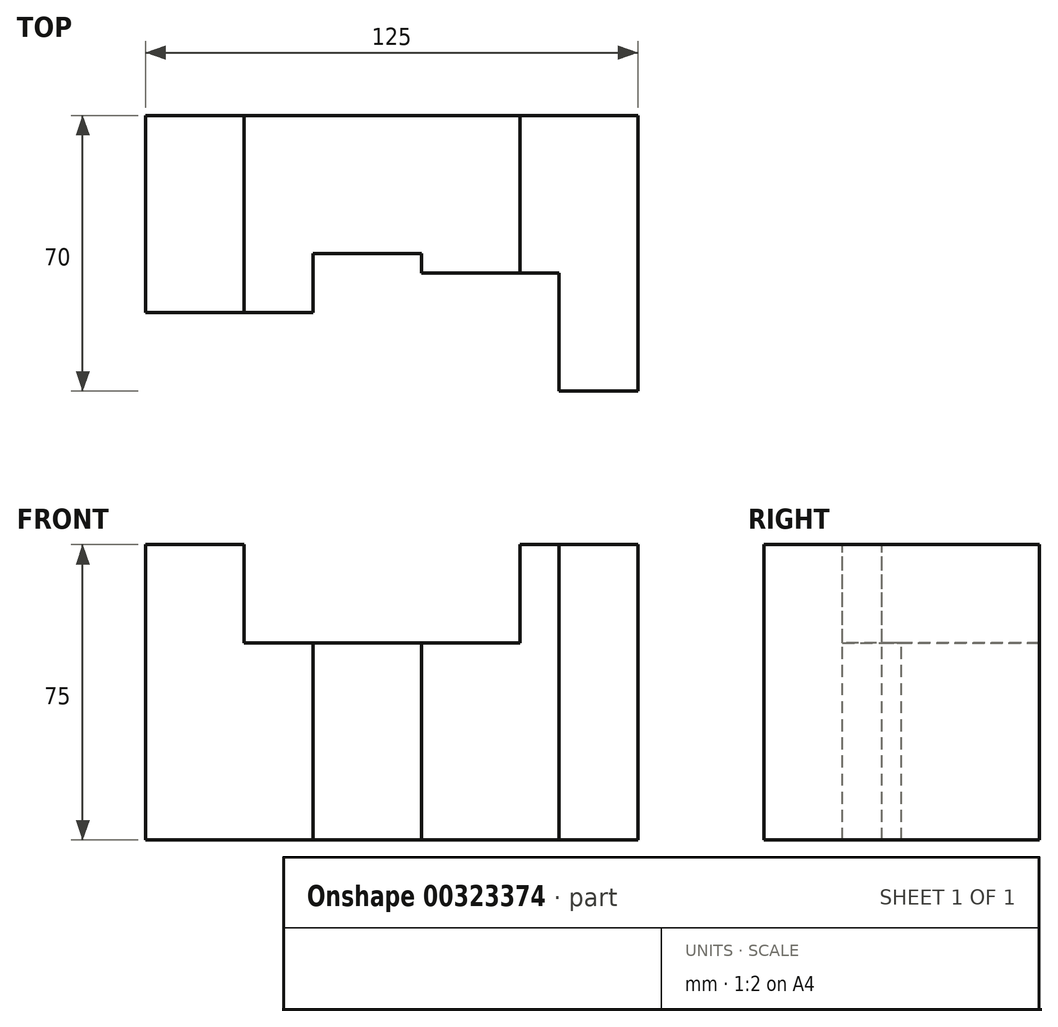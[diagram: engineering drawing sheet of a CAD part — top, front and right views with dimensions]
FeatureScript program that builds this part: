
annotation { "Feature Type Name" : "Feature", "Feature Type Description" : "" }
export const myFeature = defineFeature(function(context is Context, id is Id, definition is map)
    precondition{}
    {
        {
            var Q0;
            Q0=qCreatedBy(makeId("Top.planeOp"),FACE);
            var sketch = newSketch(context, id + "F0", { "sketchPlane" : qUnion([Q0])});
            skLineSegment(sketch, "E0", {"start": v(0, 0) * mm, "end": v(0, 50) * mm});
            skLineSegment(sketch, "E1", {"start": v(0, 50) * mm, "end": v(125, 50) * mm});
            skLineSegment(sketch, "E2", {"start": v(125, 50) * mm, "end": v(125, -20) * mm});
            skLineSegment(sketch, "E3", {"start": v(125, -20) * mm, "end": v(105, -20) * mm});
            skLineSegment(sketch, "E4", {"start": v(105, -20) * mm, "end": v(105, 10) * mm});
            skLineSegment(sketch, "E5", {"start": v(105, 10) * mm, "end": v(70, 10) * mm});
            skLineSegment(sketch, "E6", {"start": v(70, 10) * mm, "end": v(70, 15) * mm});
            skLineSegment(sketch, "E7", {"start": v(70, 15) * mm, "end": v(42.5, 15) * mm});
            skLineSegment(sketch, "E8", {"start": v(42.5, 15) * mm, "end": v(42.5, 0) * mm});
            skLineSegment(sketch, "E9", {"start": v(42.5, 0) * mm, "end": v(0, 0) * mm});
            skSolve(sketch);
        }
        {
            var Q0;
            Q0 = qSketchRegion(id + "F0", true);
            extrude(context, id + "F1", {"entities" : qUnion([Q0]), "oppositeDirection" : true, "depth" : 75 * mm});
        }
        {
            var Q0;
            Q0=qCreatedBy(makeId("Top.planeOp"),FACE);
            var sketch = newSketch(context, id + "F2", { "sketchPlane" : qUnion([Q0])});
            skLineSegment(sketch, "E10", {"start": v(25, 50) * mm, "end": v(25, 0) * mm});
            skLineSegment(sketch, "E11", {"start": v(25, 0) * mm, "end": v(42.5, 0) * mm});
            skLineSegment(sketch, "E12", {"start": v(42.5, 0) * mm, "end": v(42.5, 15) * mm});
            skLineSegment(sketch, "E13", {"start": v(42.5, 15) * mm, "end": v(70, 15) * mm});
            skLineSegment(sketch, "E14", {"start": v(70, 15) * mm, "end": v(70, 10) * mm});
            skLineSegment(sketch, "E15", {"start": v(70, 10) * mm, "end": v(95, 10) * mm});
            skLineSegment(sketch, "E16", {"start": v(95, 10) * mm, "end": v(95, 50) * mm});
            skLineSegment(sketch, "E17", {"start": v(95, 50) * mm, "end": v(25, 50) * mm});
            skSolve(sketch);
        }
        {
            var Q0;
            Q0 = qSketchRegion(id + "F2", true);
            extrude(context, id + "F3", {"entities" : qUnion([Q0]), "operationType" : NewBodyOperationType.REMOVE, "oppositeDirection" : true, "depth" : 25 * mm});
        }
    });
